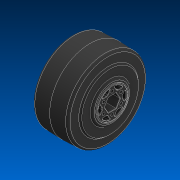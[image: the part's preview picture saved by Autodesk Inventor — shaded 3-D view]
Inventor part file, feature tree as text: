
AUTODESK INVENTOR PART (.ipt)
format: ipt  version: 2022.2 (Build 262287000, 287)  size: 1,205,760 bytes
history: native  units: in
note: dims shown in document units (in); Inventor stores cm internally (conversion verified against a paired STEP export)
features: revolve x1
ambient origin geometry x8: Origin, YZ Plane, XZ Plane, XY Plane, X Axis, Y Axis, Z Axis, Center Point
bodies: Solid1 (feature_tree)
feature tree (1):
  revolve  "Revolve1"  [1 undecoded]
note: 1 required parameter value undecoded (feature->parameter linkage not recoverable at this tier; creation-order binding heuristic only, values carry confidence <= 0.55)
